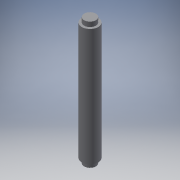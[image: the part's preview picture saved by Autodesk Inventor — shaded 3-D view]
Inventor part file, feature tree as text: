
AUTODESK INVENTOR PART (.ipt)
format: ipt  version: 2018.3 (Build 223284000, 284)  size: 95,744 bytes
history: native  units: mm
features: extrude x3, sketch x3
ambient origin geometry x8: Origin, YZ Plane, XZ Plane, XY Plane, X Axis, Y Axis, Z Axis, Center Point
bodies: Solid1 (feature_tree)
feature tree (6):
  extrude  "Extrusion1"  Depth=50.0mm TaperAngle=0.0deg
  extrude  "Extrusion2"  Depth=2.0mm TaperAngle=0.0deg
  extrude  "Extrusion3"  [1 undecoded]
  sketch  "Sketch1"  dims[d0=7.0mm d1=50.0mm d2=0.0mm]
  sketch  "Sketch2"  dims[d3=4.99mm d4=2.0mm d5=0.0mm]
  sketch  "Sketch3"  dims[d6=2.0mm d7=0.0mm]
note: 1 required parameter value undecoded (feature->parameter linkage not recoverable at this tier; creation-order binding heuristic only, values carry confidence <= 0.55)
